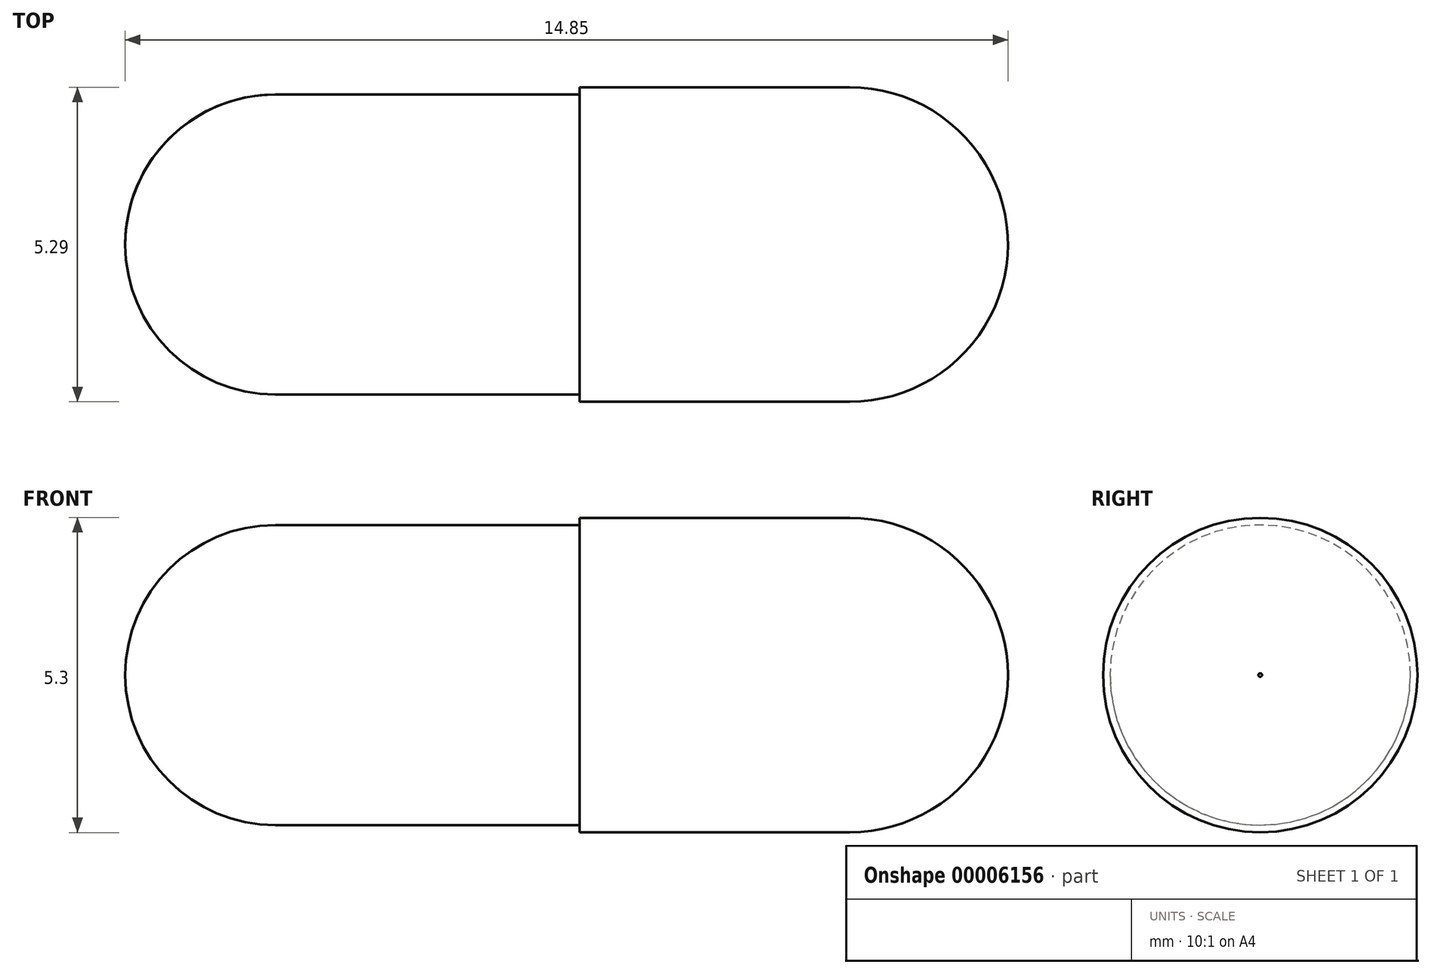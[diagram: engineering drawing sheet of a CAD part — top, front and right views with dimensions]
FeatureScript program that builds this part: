
annotation { "Feature Type Name" : "Feature", "Feature Type Description" : "" }
export const myFeature = defineFeature(function(context is Context, id is Id, definition is map)
    precondition{}
    {
        {
            var Q0;
            Q0=qCreatedBy(makeId("Top.planeOp"),FACE);
            var sketch = newSketch(context, id + "F0", { "sketchPlane" : qUnion([Q0])});
            skLineSegment(sketch, "E0.bottom", {"start": v(-6.42, 4.36) * mm, "end": v(3.24, 4.36) * mm});
            skLineSegment(sketch, "E0.right", {"start": v(3.24, 4.36) * mm, "end": v(3.24, 1.82) * mm});
            skArc(sketch, "E1", {"start": v(-6.42, 4.36) * mm, "mid": v(-8.2, 3.62) * mm, "end": v(-8.95, 1.83) * mm});
            skLineSegment(sketch, "E2", {"start": v(-1.3, 4.48) * mm, "end": v(3.24, 4.48) * mm});
            skArc(sketch, "E3", {"start": v(5.9, 1.83) * mm, "mid": v(5.12, 3.7) * mm, "end": v(3.24, 4.48) * mm});
            skLineSegment(sketch, "E4", {"start": v(-1.3, 4.48) * mm, "end": v(-1.3, 1.83) * mm});
            skLineSegment(sketch, "E5", {"start": v(-8.95, 1.83) * mm, "end": v(5.9, 1.83) * mm});
            skPoint(sketch, "E6.end.orphan", {"position": v(-1.3, -0.84) * mm});
            skPoint(sketch, "E6.start.orphan", {"position": v(3.24, -0.84) * mm});
            skSolve(sketch);
        }
        {
            var Q0;
            {var subQ3=sQuery(id+"F0.wireOp",EDGE,"E1");Q0=makeQuery(id+"F0.imprint","IMPRINT",FACE,{"disambiguationData":[TD([[makeQuery(id+"F0.imprint","IMPRINT",EDGE,{"derivedFrom":subQ3}),1.0]])]});}
            var Q1;
            {var subQ1=sQuery(id+"F0.wireOp",EDGE,"E0.right");var subQ5=sQuery(id+"F0.wireOp",EDGE,"E0.bottom");var subQ7=makeQuery(id+"F0.imprint","INTERSECT",VERTEX,{"derivedFrom":[subQ5,subQ1]});Q1=makeQuery(id+"F0.imprint","IMPRINT",FACE,{"disambiguationData":[TD([[makeQuery(id+"F0.imprint","IMPRINT",EDGE,{"disambiguationData":[TD([[subQ7,1.0]])],"derivedFrom":subQ5}),-1.0]])]});}
            var Q2;
            {var subQ7=sQuery(id+"F0.wireOp",EDGE,"E2");Q2=makeQuery(id+"F0.imprint","IMPRINT",FACE,{"disambiguationData":[TD([[makeQuery(id+"F0.imprint","IMPRINT",EDGE,{"derivedFrom":subQ7}),-1.0]])]});}
            var Q3;
            Q3=sQuery(id+"F0.wireOp",EDGE,"E5");
            revolve(context, id + "F1", {"entities" : qUnion([Q0, Q1, Q2]), "axis" : qUnion([Q3]), "revolveType" : RevolveType.FULL});
        }
    });
